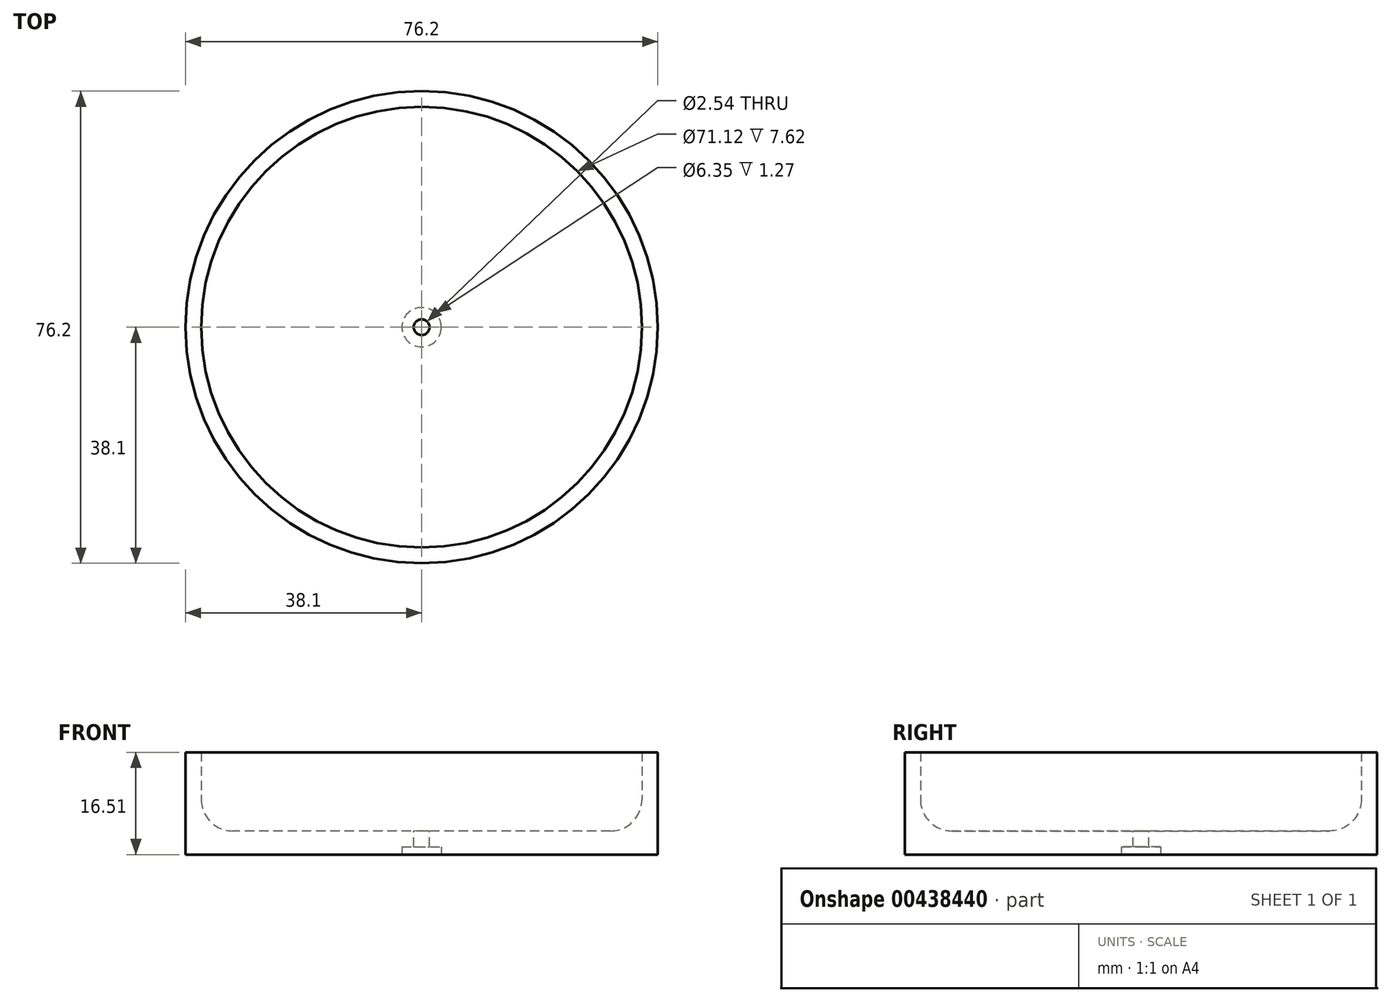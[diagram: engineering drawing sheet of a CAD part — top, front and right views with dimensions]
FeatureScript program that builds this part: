
annotation { "Feature Type Name" : "Feature", "Feature Type Description" : "" }
export const myFeature = defineFeature(function(context is Context, id is Id, definition is map)
    precondition{}
    {
        {
            var Q0;
            Q0=qCreatedBy(makeId("Top.planeOp"),FACE);
            var sketch = newSketch(context, id + "F0", { "sketchPlane" : qUnion([Q0])});
            skCircle(sketch, "E0", {"center": v(0, 0) * mm, "radius": 38.1 * mm});
            skSolve(sketch);
        }
        {
            var Q0;
            Q0 = qSketchRegion(id + "F0", true);
            extrude(context, id + "F1", {"entities" : qUnion([Q0]), "depth" : 3.8 * mm});
        }
        {
            var Q0;
            Q0=makeQuery(id+"F1.opExtrude","CAP_FACE",FACE,{"disambiguationData":[OSD([sQuery(id+"F0.wireOp",EDGE,"E0")])],"isStart":false});
            var sketch = newSketch(context, id + "F2", { "sketchPlane" : qUnion([Q0])});
            skCircle(sketch, "E1", {"center": v(0, 0) * mm, "radius": 38.1 * mm});
            skCircle(sketch, "E2", {"center": v(0, 0) * mm, "radius": 35.56 * mm});
            skSolve(sketch);
        }
        {
            var Q0;
            Q0 = qSketchRegion(id + "F2", true);
            extrude(context, id + "F3", {"entities" : qUnion([Q0]), "operationType" : NewBodyOperationType.ADD, "depth" : 12.7 * mm});
        }
        {
            var Q0;
            Q0=makeQuery(id+"F1.opExtrude","CAP_FACE",FACE,{"disambiguationData":[OSD([sQuery(id+"F0.wireOp",EDGE,"E0")])],"isStart":false});
            fillet(context, id + "F4", {"entities" : qUnion([Q0]), "radius" : 5.08 * mm, "tangentPropagation" : true, "allowEdgeOverflow" : false});
        }
        {
            var Q0;
            Q0=makeQuery(id+"F1.opExtrude","CAP_FACE",FACE,{"disambiguationData":[OSD([sQuery(id+"F0.wireOp",EDGE,"E0")])],"isStart":false});
            var sketch = newSketch(context, id + "F5", { "sketchPlane" : qUnion([Q0])});
            skCircle(sketch, "E3", {"center": v(0, 0) * mm, "radius": 1.27 * mm});
            skSolve(sketch);
        }
        {
            var Q0;
            Q0 = qSketchRegion(id + "F5", true);
            extrude(context, id + "F6", {"entities" : qUnion([Q0]), "operationType" : NewBodyOperationType.REMOVE, "oppositeDirection" : true, "depth" : 25.4 * mm});
        }
        {
            var Q0;
            Q0=makeQuery(id+"F1.opExtrude","CAP_FACE",FACE,{"disambiguationData":[OSD([sQuery(id+"F0.wireOp",EDGE,"E0")])],"isStart":true});
            var sketch = newSketch(context, id + "F7", { "sketchPlane" : qUnion([Q0])});
            skCircle(sketch, "E4", {"center": v(0, 0) * mm, "radius": 3.18 * mm});
            skSolve(sketch);
        }
        {
            var Q0;
            Q0 = qSketchRegion(id + "F7", true);
            extrude(context, id + "F8", {"entities" : qUnion([Q0]), "operationType" : NewBodyOperationType.REMOVE, "oppositeDirection" : true, "depth" : 1.27 * mm});
        }
    });
